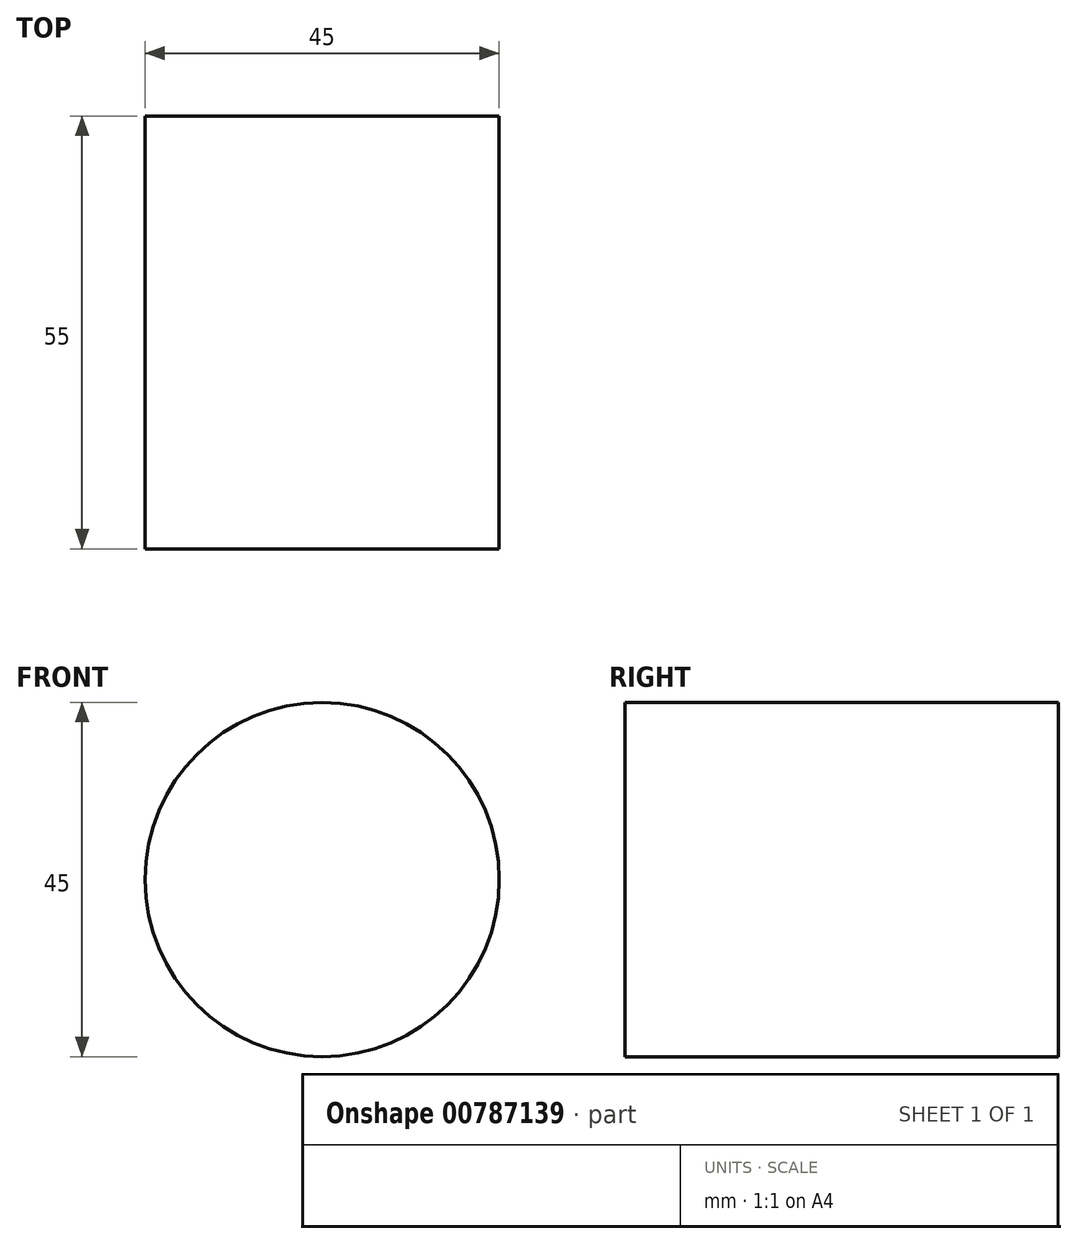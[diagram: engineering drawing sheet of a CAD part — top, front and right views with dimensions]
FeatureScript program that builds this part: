
annotation { "Feature Type Name" : "Feature", "Feature Type Description" : "" }
export const myFeature = defineFeature(function(context is Context, id is Id, definition is map)
    precondition{}
    {
        {
            var Q0;
            Q0=qCreatedBy(makeId("Front.planeOp"),FACE);
            var sketch = newSketch(context, id + "F0", { "sketchPlane" : qUnion([Q0])});
            skCircle(sketch, "E0", {"center": v(0, 0) * mm, "radius": 22.5 * mm});
            skSolve(sketch);
        }
        {
            var Q0;
            Q0=makeQuery(id+"F0.imprint","IMPRINT",FACE,{"disambiguationData":[TD([[makeQuery(id+"F0.imprint","IMPRINT",EDGE,{"derivedFrom":sQuery(id+"F0.wireOp",EDGE,"E0")}),1.0]])]});
            extrude(context, id + "F1", {"entities" : qUnion([Q0]), "depth" : 55 * mm, "offsetDistance" : 25 * mm});
        }
    });
